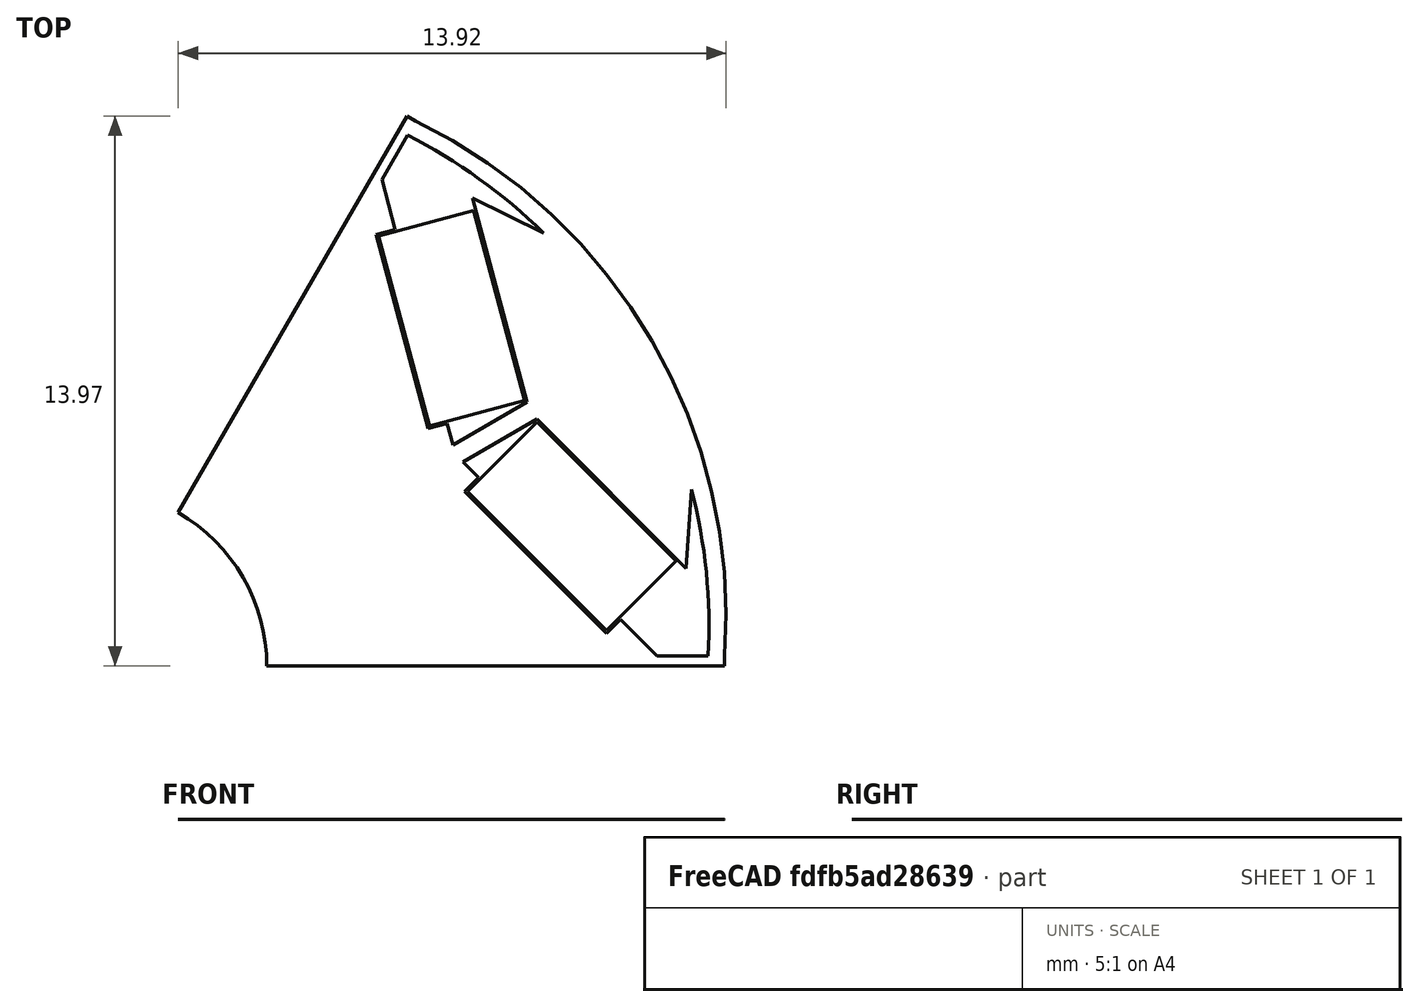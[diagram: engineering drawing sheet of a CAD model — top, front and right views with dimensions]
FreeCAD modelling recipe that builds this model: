
FCSTD DOCUMENT  (FreeCAD 0.18R4 (GitTag))
Label: vrotor
License: All rights reserved
LicenseURL: http://en.wikipedia.org/wiki/All_rights_reserved
objects: Sketcher::SketchObject×7, Surface::Filling×7, PartDesign::Body×2, Part::Cut×2, Spreadsheet::Sheet×1, Part::MultiFuse×1
note: 19 computed .brp shape members not serialized (recipe doc carries the construction recipe); baked Part::Feature solids carry a one-line shape summary decoded from their .brp

FEATURE [Spreadsheet::Sheet] Spreadsheet  label="Variables"
  cells = A2=poleNumber; B2(poleNumber)=6; A3=outerDiameter; B3(outerDiameter)=33; D3=Calc Value; A4=innerDiameter; B4(innerDiameter)=9; D4=Input Value; A5=stackLength; B5(stackLength)=20; D5=Used; A6=stackingFactor; B6(stackingFactor)=0.95; A7=embrace; B7(embrace)=70; A8=contourRatio; B8(contourRatio)=85; A9=magnetAirgap; B9(magnetAirgap)=0.05; A10=poleSeparation; B10(poleSeparation)=0.5; A11=magnetWidth; B11(magnetWidth)=5; A12=magnetHeight; B12(magnetHeight)=2.5; A13=rib; B13(rib)=0.5; A14=bridgeCurved; B14(bridgeCurved)=0.5; A15=cutTop; B15(cutTop)=0.01; A16=cutBottom; B16(cutBottom)=0.5; A17=segmentAngle; B17(segmentAngle)==360 / poleNumber; A18=movePocketInwards; B18(movePocketInwards)=0.5; A19=cuttingThickness; B19(cuttingThickness)=0.1; A20=magnetLength; B20(magnetLength)==stackLength; A21=cut; B21(cut)=0.2; A22=ribShaft; B22(ribShaft)=0.5; A23=magnetEmbrace; B23(magnetEmbrace)=75; A24=magnetContourRatio; B24(magnetContourRatio)=95; A25=axialMisalignment; B25(axialMisalignment)=0.5; A26=magnetAngle; B26(magnetAngle)=150; A27=magnetContactRatio; B27(magnetContactRatio)=65
FEATURE [Sketcher::SketchObject] Sketch003  label="RotorPoleSketch"
  MapMode = 5
  Support = -> [XY_Plane]
  expr: Constraints[14] = Variables.innerDiameter / 2
  expr: Constraints[55] = Variables.outerDiameter / 2 * Variables.contourRatio / 100
  expr: Constraints[73] = Variables.movePocketInwards
  expr: Constraints[59] = Variables.poleSeparation / 2
  expr: Constraints[106] = Variables.magnetHeight + 2 * Variables.magnetAirgap
  expr: Constraints[23] = Variables.outerDiameter / 2 * Variables.contourRatio / 100
  expr: Constraints[90] = Variables.cutTop
  expr: Constraints[71] = Variables.segmentAngle * Variables.embrace / 100
  expr: Constraints[15] = Variables.outerDiameter / 2
  expr: Constraints[103] = Variables.cutBottom
  expr: Constraints[58] = Variables.bridgeCurved
  expr: Constraints[114] = Variables.outerDiameter / 2 * Variables.contourRatio / 100 - Variables.bridgeCurved
  expr: Constraints[51] = Variables.rib / 2
  expr: Constraints[43] = Variables.rib / 2
  expr: Constraints[0] = Variables.segmentAngle
  expr: Constraints[18] = Variables.segmentAngle / 2
  expr: Constraints[91] = Variables.magnetWidth + Variables.magnetAirgap * 2
  expr: Constraints[116] = Variables.outerDiameter / 2 * Variables.contourRatio / 100 - Variables.bridgeCurved
  expr: Constraints[27] = Variables.poleSeparation / 2
  sketch-geometry (40):
    g0: LineSegment [constr] StartX=4.5 StartY=0 StartZ=0 EndX=16.5 EndY=0 EndZ=0
    g1: LineSegment [constr] StartX=2.25 StartY=3.89711 StartZ=0 EndX=8.25 EndY=14.2894 EndZ=0
    g2: LineSegment [constr] StartX=0 StartY=0 StartZ=0 EndX=4.5 EndY=0 EndZ=0
    g3: LineSegment [constr] StartX=0 StartY=0 StartZ=0 EndX=2.25 EndY=3.89711 EndZ=0
    g4: ArcOfCircle [constr] CenterX=0 CenterY=0 CenterZ=0 NormalX=0 NormalY=0 NormalZ=1 AngleXU=0 Radius=16.5 StartAngle=0 EndAngle=1.0472
    g5: ArcOfCircle CenterX=0 CenterY=0 CenterZ=0 NormalX=0 NormalY=0 NormalZ=1 AngleXU=0 Radius=4.5 StartAngle=0 EndAngle=1.0472
    g6: LineSegment [constr] StartX=0 StartY=0 StartZ=0 EndX=14.2894 EndY=8.25 EndZ=0
    g7: ArcOfCircle [constr] CenterX=2.14341 CenterY=1.2375 CenterZ=0 NormalX=0 NormalY=0 NormalZ=1 AngleXU=0 Radius=14.025 StartAngle=6.19484 EndAngle=7.41873
    g8: LineSegment StartX=8.0668 StartY=13.9721 StartZ=0 EndX=8.28331 EndY=13.8471 EndZ=0
    g9: LineSegment StartX=16.1336 StartY=0 StartZ=0 EndX=16.1336 EndY=0.25 EndZ=0
    g10: ArcOfCircle CenterX=2.14341 CenterY=1.2375 CenterZ=0 NormalX=0 NormalY=0 NormalZ=1 AngleXU=0 Radius=14.025 StartAngle=6.21272 EndAngle=7.40085
    g11: LineSegment StartX=2.25 StartY=3.89711 StartZ=0 EndX=8.0668 EndY=13.9721 EndZ=0
    g12: LineSegment StartX=4.5 StartY=0 StartZ=0 EndX=16.1336 EndY=0 EndZ=0
    g13: LineSegment [constr] StartX=8.46556 StartY=14.1628 StartZ=0 EndX=2.46303 EndY=3.7661 EndZ=0
    g14: LineSegment [constr] StartX=2.46303 StartY=3.7661 StartZ=0 EndX=2.24653 EndY=3.8911 EndZ=0
    g15: LineSegment [constr] StartX=4.49305 StartY=0.25 StartZ=0 EndX=16.4981 EndY=0.25 EndZ=0
    g16: LineSegment [constr] StartX=4.49305 StartY=0.25 StartZ=0 EndX=4.49305 EndY=0 EndZ=0
    g17: ArcOfCircle [constr] CenterX=1.7104 CenterY=0.9875 CenterZ=0 NormalX=0 NormalY=0 NormalZ=1 AngleXU=0 Radius=14.025 StartAngle=6.21272 EndAngle=7.40085
    g18: LineSegment [constr] StartX=2.14341 StartY=1.2375 StartZ=0 EndX=1.7104 EndY=0.9875 EndZ=0
    g19: LineSegment [constr] StartX=15.6558 StartY=2.47964 StartZ=0 EndX=15.1558 EndY=2.47964 EndZ=0
    g20: LineSegment [constr] StartX=15.1558 StartY=2.47964 StartZ=0 EndX=9.72533 EndY=11.8855 EndZ=0
    g21: LineSegment [constr] StartX=9.72533 StartY=11.8855 StartZ=0 EndX=9.97533 EndY=12.3185 EndZ=0
    g22: LineSegment [constr] StartX=0 StartY=0 StartZ=0 EndX=15.6558 EndY=2.47964 EndZ=0
    g23: LineSegment [constr] StartX=0 StartY=0 StartZ=0 EndX=9.97533 EndY=12.3185 EndZ=0
    g24: ArcOfCircle [constr] CenterX=2.00505 CenterY=1.39146 CenterZ=0 NormalX=0 NormalY=0 NormalZ=1 AngleXU=0 Radius=13.525 StartAngle=0.940605 EndAngle=1.10569
    g25: ArcOfCircle [constr] CenterX=2.20756 CenterY=1.0407 CenterZ=0 NormalX=0 NormalY=0 NormalZ=1 AngleXU=0 Radius=13.525 StartAngle=6.22469 EndAngle=6.38978
    g26: LineSegment [constr] StartX=9.72533 StartY=11.8855 StartZ=0 EndX=11.1656 EndY=9.39093 EndZ=0
    g27: LineSegment [constr] StartX=11.1656 StartY=9.39093 StartZ=0 EndX=11.1742 EndY=9.39593 EndZ=0
    g28: LineSegment [constr] StartX=11.1742 StartY=9.39593 StartZ=0 EndX=13.7242 EndY=4.9792 EndZ=0
    g29: LineSegment [constr] StartX=13.7242 StartY=4.9792 StartZ=0 EndX=13.7156 EndY=4.9742 EndZ=0
    g30: LineSegment [constr] StartX=13.7156 StartY=4.9742 StartZ=0 EndX=15.1558 EndY=2.47964 EndZ=0
    g31: LineSegment [constr] StartX=7.23138 StartY=12.0251 StartZ=0 EndX=14.0298 EndY=0.25 EndZ=0
    g32: LineSegment [constr] StartX=9.35557 StartY=8.34593 StartZ=0 EndX=8.92256 EndY=8.09593 EndZ=0
    g33: LineSegment [constr] StartX=8.92256 StartY=8.09593 StartZ=0 EndX=11.4726 EndY=3.6792 EndZ=0
    g34: LineSegment [constr] StartX=11.4726 StartY=3.6792 StartZ=0 EndX=11.9056 EndY=3.9292 EndZ=0
    g35: LineSegment [constr] StartX=11.4726 StartY=3.6792 StartZ=0 EndX=13.7242 EndY=4.9792 EndZ=0
    g36: LineSegment [constr] StartX=9.35557 StartY=8.34593 StartZ=0 EndX=7.23138 EndY=12.0251 EndZ=0
    g37: LineSegment [constr] StartX=11.9056 StartY=3.9292 StartZ=0 EndX=14.0298 EndY=0.25 EndZ=0
    g38: LineSegment [constr] StartX=7.23138 StartY=12.0251 StartZ=0 EndX=8.07122 EndY=13.4798 EndZ=0
    g39: LineSegment [constr] StartX=14.0298 StartY=0.25 StartZ=0 EndX=15.7094 EndY=0.25 EndZ=0
  constraints (117):
    c: Angle(g0,g1) = 1.0472
    c: Coincident(g2,g-1)
    c: Coincident(g2,g0)
    c: Coincident(g3,g2)
    c: Coincident(g3,g1)
    c: Parallel(g2,g0)
    c: Parallel(g3,g1)
    c: Coincident(g4,g-1)
    c: Coincident(g4,g0)
    c: Coincident(g4,g1)
    c: Coincident(g5,g4)
    c: Coincident(g5,g1)
    c: Coincident(g5,g0)
    c: Angle(g-1,g2) = 0
    c: Radius(g5) = 4.5
    c: Radius(g4) = 16.5
    c: Coincident(g6,g5)
    c: PointOnObject(g6,g4)
    c: Angle(g-1,g6) = 0.523599
    c: PointOnObject(g7,g1)
    c: PointOnObject(g7,g0)
    c: PointOnObject(g6,g7)
    c: PointOnObject(g7,g6)
    c: Radius(g7) = 14.025
    c: PointOnObject(g8,g1)
    c: PointOnObject(g8,g7)
    c: Angle(g1,g8) = 1.5708
    c: Distance(g8) = 0.25
    c: PointOnObject(g9,g0)
    c: PointOnObject(g9,g7)
    c: Angle(g9,g0) = 1.5708
    c: Coincident(g10,g8)
    c: Coincident(g10,g9)
    c: PointOnObject(g6,g10)
    c: Coincident(g11,g5)
    c: Coincident(g11,g8)
    c: Coincident(g12,g5)
    c: Coincident(g12,g9)
    c: PointOnObject(g13,g4)
    c: PointOnObject(g13,g5)
    c: Coincident(g14,g13)
    c: PointOnObject(g14,g11)
    c: Angle(g13,g14) = 1.5708
    c: Distance(g14) = 0.25
    c: Parallel(g11,g13)
    c: PointOnObject(g15,g5)
    c: PointOnObject(g15,g4)
    c: Parallel(g15,g2)
    c: Coincident(g16,g15)
    c: PointOnObject(g16,g2)
    c: Angle(g16,g15) = 1.5708
    c: Distance(g16) = 0.25
    c: PointOnObject(g17,g6)
    c: PointOnObject(g17,g11)
    c: PointOnObject(g17,g12)
    c: Radius(g17) = 14.025
    c: Coincident(g18,g10)
    c: Coincident(g18,g17)
    c: Distance(g17,g10) = 0.5
    c: DistanceY(g9,g9) = 0.25
    c: PointOnObject(g38,g13)
    c: PointOnObject(g39,g15)
    c: PointOnObject(g19,g17)
    c: Horizontal(g19)
    c: Coincident(g20,g19)
    c: Coincident(g21,g20)
    c: Coincident(g22,g5)
    c: Coincident(g22,g19)
    c: Coincident(g23,g5)
    c: Coincident(g23,g21)
    c: Symmetric(g21,g19,g6)
    c: Angle(g22,g23) = 0.733038
    c: Parallel(g21,g11)
    c: DistanceX(g19,g19) = 0.5
    c: Equal(g19,g21)
    c: Coincident(g24,g21)
    c: Tangent(g24,g17)
    c: Coincident(g25,g19)
    c: Tangent(g25,g17)
    c: Coincident(g26,g21)
    c: PointOnObject(g26,g20)
    c: Coincident(g27,g26)
    c: Coincident(g28,g27)
    c: Coincident(g29,g28)
    c: Coincident(g30,g29)
    c: Coincident(g30,g19)
    c: Angle(g29,g20) = 1.5708
    c: Perpendicular(g29,g28)
    c: Angle(g27,g28) = 1.5708
    c: Symmetric(g29,g26,g6)
    c: Distance(g27) = 0.01
    c: Distance(g28) = 5.1
    c: PointOnObject(g31,g13)
    c: PointOnObject(g31,g15)
    c: Parallel(g31,g20)
    c: PointOnObject(g32,g31)
    c: Coincident(g33,g32)
    c: Coincident(g34,g33)
    c: PointOnObject(g34,g31)
    c: Angle(g33,g32) = 1.5708
    c: Angle(g34,g33) = 1.5708
    c: Symmetric(g32,g33,g6)
    c: Equal(g33,g28)
    c: Distance(g34) = 0.5
    c: Coincident(g35,g33)
    c: Coincident(g35,g28)
    c: Distance(g35) = 2.6
    c: Coincident(g36,g32)
    c: Coincident(g36,g31)
    c: Coincident(g37,g34)
    c: Coincident(g37,g31)
    c: Coincident(g38,g36)
    c: Coincident(g39,g37)
    c: Coincident(g24,g38)
    c: Radius(g24) = 13.525
    c: Coincident(g25,g39)
    c: Radius(g25) = 13.525
FEATURE [Sketcher::SketchObject] Sketch004  label="BoundingBox"
  MapMode = 5
  Support = -> [XY_Plane]
  expr: Constraints[8] = Variables.outerDiameter
  sketch-geometry (6):
    g0: LineSegment StartX=-16.5 StartY=-16.5 StartZ=0 EndX=16.5 EndY=-16.5 EndZ=0
    g1: LineSegment StartX=16.5 StartY=-16.5 StartZ=0 EndX=16.5 EndY=16.5 EndZ=0
    g2: LineSegment StartX=16.5 StartY=16.5 StartZ=0 EndX=-16.5 EndY=16.5 EndZ=0
    g3: LineSegment StartX=-16.5 StartY=16.5 StartZ=0 EndX=-16.5 EndY=-16.5 EndZ=0
    g4: LineSegment [constr] StartX=-16.5 StartY=-16.5 StartZ=0 EndX=16.5 EndY=16.5 EndZ=0
    g5: GeomPoint X=0 Y=0 Z=0
  constraints (14):
    c: Coincident(g0,g1)
    c: Coincident(g1,g2)
    c: Coincident(g2,g3)
    c: Coincident(g3,g0)
    c: Horizontal(g0)
    c: Horizontal(g2)
    c: Vertical(g1)
    c: Vertical(g3)
    c: DistanceY(g1,g1) = 33
    c: Equal(g2,g1)
    c: Coincident(g4,g0)
    c: Coincident(g4,g1)
    c: Symmetric(g0,g1,g5)
    c: Coincident(g-1,g5)
FEATURE [Sketcher::SketchObject] Sketch005  label="RotorSideSketch"
  MapMode = 5
  Support = -> [XY_Plane001]
  expr: Constraints[23] = Variables.stackLength / 2 - Variables.axialMisalignment
  expr: Constraints[19] = Variables.innerDiameter / 2
  expr: Constraints[22] = Variables.stackLength / 2 - Variables.axialMisalignment
  expr: Constraints[9] = Variables.outerDiameter / 2
  expr: Constraints[8] = Variables.innerDiameter / 2
  expr: Constraints[7] = Variables.stackLength
  sketch-geometry (8):
    g0: LineSegment StartX=-9.5 StartY=4.5 StartZ=0 EndX=10.5 EndY=4.5 EndZ=0
    g1: LineSegment StartX=10.5 StartY=4.5 StartZ=0 EndX=10.5 EndY=16.5 EndZ=0
    g2: LineSegment StartX=10.5 StartY=16.5 StartZ=0 EndX=-9.5 EndY=16.5 EndZ=0
    g3: LineSegment StartX=-9.5 StartY=16.5 StartZ=0 EndX=-9.5 EndY=4.5 EndZ=0
    g4: LineSegment StartX=-9.5 StartY=-4.5 StartZ=0 EndX=10.5 EndY=-4.5 EndZ=0
    g5: LineSegment StartX=10.5 StartY=-4.5 StartZ=0 EndX=10.5 EndY=-16.5 EndZ=0
    g6: LineSegment StartX=10.5 StartY=-16.5 StartZ=0 EndX=-9.5 EndY=-16.5 EndZ=0
    g7: LineSegment StartX=-9.5 StartY=-16.5 StartZ=0 EndX=-9.5 EndY=-4.5 EndZ=0
  constraints (24):
    c: Coincident(g0,g1)
    c: Coincident(g1,g2)
    c: Coincident(g2,g3)
    c: Coincident(g3,g0)
    c: Horizontal(g0)
    c: Vertical(g1)
    c: Vertical(g3)
    c: DistanceX(g2,g2) = 20
    c: DistanceY(g-1,g0) = 4.5
    c: DistanceY(g-1,g1) = 16.5
    c: Coincident(g4,g5)
    c: Coincident(g5,g6)
    c: Coincident(g6,g7)
    c: Coincident(g7,g4)
    c: Horizontal(g4)
    c: Vertical(g5)
    c: Vertical(g7)
    c: Equal(g4,g0)
    c: Equal(g7,g3)
    c: DistanceY(g4,g-1) = 4.5
    c: Horizontal(g2)
    c: Horizontal(g6)
    c: DistanceX(g0,g-1) = 9.5
    c: DistanceX(g4,g-1) = 9.5
FEATURE [Sketcher::SketchObject] Sketch006  label="MagnetSideSketch"
  ExternalGeometry = -> [Sketch005]
  MapMode = 5
  Support = -> [XY_Plane001]
  expr: Constraints[23] = Variables.stackLength / 2 - Variables.axialMisalignment
  expr: Constraints[12] = Variables.magnetHeight / 2
  expr: Constraints[8] = Variables.magnetHeight
  expr: Constraints[7] = Variables.magnetLength
  sketch-geometry (9):
    g0: LineSegment StartX=-9.5 StartY=12.75 StartZ=0 EndX=10.5 EndY=12.75 EndZ=0
    g1: LineSegment StartX=10.5 StartY=12.75 StartZ=0 EndX=10.5 EndY=15.25 EndZ=0
    g2: LineSegment StartX=10.5 StartY=15.25 StartZ=0 EndX=-9.5 EndY=15.25 EndZ=0
    g3: LineSegment StartX=-9.5 StartY=15.25 StartZ=0 EndX=-9.5 EndY=12.75 EndZ=0
    g4: LineSegment [constr] StartX=10.5 StartY=15.25 StartZ=0 EndX=10.5 EndY=16.5 EndZ=0
    g5: LineSegment StartX=-9.5 StartY=-15.25 StartZ=0 EndX=10.5 EndY=-15.25 EndZ=0
    g6: LineSegment StartX=10.5 StartY=-15.25 StartZ=0 EndX=10.5 EndY=-12.75 EndZ=0
    g7: LineSegment StartX=10.5 StartY=-12.75 StartZ=0 EndX=-9.5 EndY=-12.75 EndZ=0
    g8: LineSegment StartX=-9.5 StartY=-12.75 StartZ=0 EndX=-9.5 EndY=-15.25 EndZ=0
  constraints (25):
    c: Coincident(g0,g1)
    c: Coincident(g1,g2)
    c: Coincident(g2,g3)
    c: Coincident(g3,g0)
    c: Horizontal(g0)
    c: Vertical(g1)
    c: Vertical(g3)
    c: DistanceX(g2,g2) = 20
    c: DistanceY(g1,g1) = 2.5
    c: Coincident(g4,g1)
    c: PointOnObject(g4,g-3)
    c: Angle(g4,g2) = 1.5708
    c: DistanceY(g4,g4) = 1.25
    c: Coincident(g5,g6)
    c: Coincident(g6,g7)
    c: Coincident(g7,g8)
    c: Coincident(g8,g5)
    c: Horizontal(g5)
    c: Vertical(g6)
    c: Vertical(g8)
    c: Symmetric(g7,g0,g-1)
    c: Symmetric(g6,g0,g-1)
    c: Equal(g8,g3)
    c: DistanceX(g0,g-1) = 9.5
    c: Horizontal(g2)
FEATURE [PartDesign::Body] Body001  label="SideView"
  Group = -> [Sketch005,Sketch006]
  Origin = -> Origin001
FEATURE [Surface::Filling] Surface  label="RotorPoleSketch_Surface"
  Anisotropy = false
  BoundaryEdges = -> [Sketch003]
  BoundaryOrder = [0,0,0,0,0,0]
  Degree = 3
  Iterations = 2
  MaximumDegree = 8
  MaximumSegments = 9
  PointsOnCurve = 15
  TolAngular = 0.01
  TolCurvature = 0.1
  Tolerance2d = 1e-05
  Tolerance3d = 0.0001
FEATURE [Sketcher::SketchObject] Sketch007  label="PocketSketch"
  MapMode = 5
  Support = -> [XY_Plane]
  expr: Constraints[123] = Variables.rib / 2
  expr: Constraints[93] = Variables.magnetAngle
  expr: Constraints[78] = 0.5 * Variables.segmentAngle * Variables.embrace / 100 * Variables.magnetContactRatio / 100
  expr: Constraints[51] = Variables.rib / 2
  expr: Constraints[27] = Variables.poleSeparation / 2
  expr: Constraints[14] = Variables.innerDiameter / 2
  expr: Constraints[55] = Variables.outerDiameter / 2 * Variables.contourRatio / 100
  expr: Constraints[115] = Variables.cutBottom
  expr: Constraints[103] = Variables.magnetHeight + Variables.magnetAirgap * 2 - Variables.cutBottom
  expr: Constraints[58] = Variables.bridgeCurved
  expr: Constraints[69] = Variables.segmentAngle * Variables.embrace / 100
  expr: Constraints[71] = Variables.movePocketInwards
  expr: Constraints[15] = Variables.outerDiameter / 2
  expr: Constraints[59] = Variables.poleSeparation / 2
  expr: Constraints[116] = Variables.magnetWidth + Variables.magnetAirgap * 2
  expr: Constraints[23] = Variables.outerDiameter / 2 * Variables.contourRatio / 100
  expr: Constraints[43] = Variables.rib / 2
  expr: Constraints[18] = Variables.segmentAngle / 2
  expr: Constraints[0] = Variables.segmentAngle
  sketch-geometry (54):
    g0: LineSegment [constr] StartX=4.5 StartY=0 StartZ=0 EndX=16.5 EndY=0 EndZ=0
    g1: LineSegment [constr] StartX=2.25 StartY=3.89711 StartZ=0 EndX=8.25 EndY=14.2894 EndZ=0
    g2: LineSegment [constr] StartX=0 StartY=0 StartZ=0 EndX=4.5 EndY=0 EndZ=0
    g3: LineSegment [constr] StartX=0 StartY=0 StartZ=0 EndX=2.25 EndY=3.89711 EndZ=0
    g4: ArcOfCircle [constr] CenterX=0 CenterY=0 CenterZ=0 NormalX=0 NormalY=0 NormalZ=1 AngleXU=0 Radius=16.5 StartAngle=0 EndAngle=1.0472
    g5: ArcOfCircle [constr] CenterX=0 CenterY=0 CenterZ=0 NormalX=0 NormalY=0 NormalZ=1 AngleXU=0 Radius=4.5 StartAngle=0 EndAngle=1.0472
    g6: LineSegment [constr] StartX=0 StartY=0 StartZ=0 EndX=14.2894 EndY=8.25 EndZ=0
    g7: ArcOfCircle [constr] CenterX=2.14341 CenterY=1.2375 CenterZ=0 NormalX=0 NormalY=0 NormalZ=1 AngleXU=0 Radius=14.025 StartAngle=6.19484 EndAngle=7.41873
    g8: LineSegment [constr] StartX=8.0668 StartY=13.9721 StartZ=0 EndX=8.28331 EndY=13.8471 EndZ=0
    g9: LineSegment [constr] StartX=16.1336 StartY=0 StartZ=0 EndX=16.1336 EndY=0.25 EndZ=0
    g10: ArcOfCircle [constr] CenterX=2.14341 CenterY=1.2375 CenterZ=0 NormalX=0 NormalY=0 NormalZ=1 AngleXU=0 Radius=14.025 StartAngle=6.21272 EndAngle=7.40085
    g11: LineSegment [constr] StartX=2.25 StartY=3.89711 StartZ=0 EndX=8.0668 EndY=13.9721 EndZ=0
    g12: LineSegment [constr] StartX=4.5 StartY=0 StartZ=0 EndX=16.1336 EndY=0 EndZ=0
    g13: LineSegment [constr] StartX=8.46556 StartY=14.1628 StartZ=0 EndX=2.46303 EndY=3.7661 EndZ=0
    g14: LineSegment [constr] StartX=2.46303 StartY=3.7661 StartZ=0 EndX=2.24653 EndY=3.8911 EndZ=0
    g15: LineSegment [constr] StartX=4.49305 StartY=0.25 StartZ=0 EndX=16.4981 EndY=0.25 EndZ=0
    g16: LineSegment [constr] StartX=4.49305 StartY=0.25 StartZ=0 EndX=4.49305 EndY=0 EndZ=0
    g17: ArcOfCircle [constr] CenterX=1.7104 CenterY=0.9875 CenterZ=0 NormalX=0 NormalY=0 NormalZ=1 AngleXU=0 Radius=14.025 StartAngle=6.21272 EndAngle=7.40085
    g18: LineSegment [constr] StartX=2.14341 StartY=1.2375 StartZ=0 EndX=1.7104 EndY=0.9875 EndZ=0
    g19: LineSegment [constr] StartX=15.6558 StartY=2.47964 StartZ=0 EndX=15.1558 EndY=2.47964 EndZ=0
    g20: LineSegment [constr] StartX=15.1558 StartY=2.47964 StartZ=0 EndX=9.72533 EndY=11.8855 EndZ=0
    g21: LineSegment [constr] StartX=9.72533 StartY=11.8855 StartZ=0 EndX=9.97533 EndY=12.3185 EndZ=0
    g22: LineSegment [constr] StartX=0 StartY=0 StartZ=0 EndX=15.6558 EndY=2.47964 EndZ=0
    g23: LineSegment [constr] StartX=0 StartY=0 StartZ=0 EndX=9.97533 EndY=12.3185 EndZ=0
    g24: ArcOfCircle [constr] CenterX=1.7104 CenterY=0.9875 CenterZ=0 NormalX=0 NormalY=0 NormalZ=1 AngleXU=0 Radius=14.025 StartAngle=0.252123 EndAngle=0.795074
    g25: LineSegment [constr] StartX=0 StartY=0 StartZ=0 EndX=15.292 EndY=4.48618 EndZ=0
    g26: LineSegment StartX=11.5311 StartY=11.0002 StartZ=0 EndX=9.72533 EndY=11.8855 EndZ=0
    g27: LineSegment StartX=15.292 StartY=4.48618 StartZ=0 EndX=15.1558 EndY=2.47964 EndZ=0
    g28: ArcOfCircle CenterX=1.7104 CenterY=0.9875 CenterZ=0 NormalX=0 NormalY=0 NormalZ=1 AngleXU=0 Radius=14.025 StartAngle=0.795074 EndAngle=1.09981
    g29: ArcOfCircle CenterX=1.7104 CenterY=0.9875 CenterZ=0 NormalX=0 NormalY=0 NormalZ=1 AngleXU=0 Radius=14.025 StartAngle=6.23058 EndAngle=6.53531
    g30: LineSegment [constr] StartX=9.72533 StartY=11.8855 StartZ=0 EndX=11.1804 EndY=6.45502 EndZ=0
    g31: LineSegment [constr] StartX=11.1804 StartY=6.45502 StartZ=0 EndX=15.1558 EndY=2.47964 EndZ=0
    g32: LineSegment [constr] StartX=7.4243 StartY=12.3593 StartZ=0 EndX=9.29761 EndY=5.36798 EndZ=0
    g33: LineSegment [constr] StartX=9.29761 StartY=5.36798 StartZ=0 EndX=14.4156 EndY=0.25 EndZ=0
    g34: LineSegment [constr] StartX=7.4243 StartY=12.3593 StartZ=0 EndX=9.45274 EndY=12.9028 EndZ=0
    g35: LineSegment StartX=8.0745 StartY=13.4855 StartZ=0 EndX=7.4243 EndY=12.3593 EndZ=0
    g36: LineSegment StartX=7.4243 StartY=12.3593 StartZ=0 EndX=7.76501 EndY=11.0877 EndZ=0
    g37: LineSegment StartX=7.76501 StartY=11.0877 StartZ=0 EndX=7.28205 EndY=10.9583 EndZ=0
    g38: LineSegment StartX=7.28205 StartY=10.9583 StartZ=0 EndX=8.60202 EndY=6.03209 EndZ=0
    g39: LineSegment StartX=8.60202 StartY=6.03209 StartZ=0 EndX=9.08499 EndY=6.1615 EndZ=0
    g40: LineSegment StartX=9.23062 StartY=5.61798 StartZ=0 EndX=11.1134 EndY=6.70502 EndZ=0
    g41: LineSegment [constr] StartX=9.23062 StartY=5.61798 StartZ=0 EndX=9.35562 EndY=5.40147 EndZ=0
    g42: LineSegment [constr] StartX=9.08499 StartY=6.1615 StartZ=0 EndX=11.1134 EndY=6.70502 EndZ=0
    g43: LineSegment StartX=9.08499 StartY=6.1615 StartZ=0 EndX=9.23062 EndY=5.61798 EndZ=0
    g44: LineSegment StartX=9.72533 StartY=11.8855 StartZ=0 EndX=11.1134 EndY=6.70502 EndZ=0
    g45: LineSegment StartX=9.48062 StartY=5.18496 StartZ=0 EndX=9.87851 EndY=4.78708 EndZ=0
    g46: LineSegment StartX=9.87851 StartY=4.78708 StartZ=0 EndX=9.52495 EndY=4.43353 EndZ=0
    g47: LineSegment StartX=9.52495 StartY=4.43353 StartZ=0 EndX=13.1312 EndY=0.827282 EndZ=0
    g48: LineSegment StartX=14.4156 StartY=0.25 StartZ=0 EndX=14.4156 EndY=0.25 EndZ=0
    g49: LineSegment StartX=13.1312 StartY=0.827282 StartZ=0 EndX=13.4848 EndY=1.18084 EndZ=0
    g50: LineSegment StartX=13.4848 StartY=1.18084 StartZ=0 EndX=14.4156 EndY=0.25 EndZ=0
    g51: LineSegment StartX=14.4156 StartY=0.25 StartZ=0 EndX=15.716 EndY=0.25 EndZ=0
    g52: LineSegment StartX=15.1558 StartY=2.47964 StartZ=0 EndX=11.3634 EndY=6.272 EndZ=0
    g53: LineSegment StartX=11.3634 StartY=6.272 StartZ=0 EndX=9.48062 EndY=5.18496 EndZ=0
  constraints (149):
    c: Angle(g0,g1) = 1.0472
    c: Coincident(g2,g-1)
    c: Coincident(g2,g0)
    c: Coincident(g3,g2)
    c: Coincident(g3,g1)
    c: Parallel(g2,g0)
    c: Parallel(g3,g1)
    c: Coincident(g4,g-1)
    c: Coincident(g4,g0)
    c: Coincident(g4,g1)
    c: Coincident(g5,g4)
    c: Coincident(g5,g1)
    c: Coincident(g5,g0)
    c: Angle(g-1,g2) = 0
    c: Radius(g5) = 4.5
    c: Radius(g4) = 16.5
    c: Coincident(g6,g5)
    c: PointOnObject(g6,g4)
    c: Angle(g-1,g6) = 0.523599
    c: PointOnObject(g7,g1)
    c: PointOnObject(g7,g0)
    c: PointOnObject(g6,g7)
    c: PointOnObject(g7,g6)
    c: Radius(g7) = 14.025
    c: PointOnObject(g8,g1)
    c: PointOnObject(g8,g7)
    c: Angle(g1,g8) = 1.5708
    c: Distance(g8) = 0.25
    c: PointOnObject(g9,g0)
    c: PointOnObject(g9,g7)
    c: Angle(g9,g0) = 1.5708
    c: Coincident(g10,g8)
    c: Coincident(g10,g9)
    c: PointOnObject(g6,g10)
    c: Coincident(g11,g5)
    c: Coincident(g11,g8)
    c: Coincident(g12,g5)
    c: Coincident(g12,g9)
    c: PointOnObject(g13,g4)
    c: PointOnObject(g13,g5)
    c: Coincident(g14,g13)
    c: PointOnObject(g14,g11)
    c: Angle(g13,g14) = 1.5708
    c: Distance(g14) = 0.25
    c: Parallel(g11,g13)
    c: PointOnObject(g15,g5)
    c: PointOnObject(g15,g4)
    c: Parallel(g15,g2)
    c: Coincident(g16,g15)
    c: PointOnObject(g16,g2)
    c: Angle(g16,g15) = 1.5708
    c: Distance(g16) = 0.25
    c: PointOnObject(g17,g6)
    c: PointOnObject(g17,g11)
    c: PointOnObject(g17,g12)
    c: Radius(g17) = 14.025
    c: Coincident(g18,g10)
    c: Coincident(g18,g17)
    c: Distance(g17,g10) = 0.5
    c: DistanceY(g9,g9) = 0.25
    c: PointOnObject(g19,g17)
    c: Horizontal(g19)
    c: Coincident(g20,g19)
    c: Coincident(g21,g20)
    c: Coincident(g22,g5)
    c: Coincident(g22,g19)
    c: Coincident(g23,g5)
    c: Coincident(g23,g21)
    c: Symmetric(g21,g19,g6)
    c: Angle(g22,g23) = 0.733038
    c: Parallel(g21,g11)
    c: DistanceX(g19,g19) = 0.5
    c: Equal(g19,g21)
    c: PointOnObject(g24,g17)
    c: Tangent(g24,g17)
    c: Symmetric(g24,g24,g6)
    c: Coincident(g25,g-1)
    c: Coincident(g25,g24)
    c: Angle(g25,g6) = 0.238237
    c: Coincident(g26,g24)
    c: Coincident(g26,g20)
    c: Coincident(g27,g24)
    c: Coincident(g27,g19)
    c: Coincident(g28,g24)
    c: PointOnObject(g28,g13)
    c: Coincident(g28,g24)
    c: Coincident(g29,g24)
    c: PointOnObject(g29,g15)
    c: Coincident(g29,g24)
    c: Coincident(g30,g26)
    c: PointOnObject(g30,g6)
    c: Coincident(g31,g30)
    c: Coincident(g31,g27)
    c: Angle(g31,g30) = 2.61799
    c: PointOnObject(g32,g13)
    c: PointOnObject(g32,g6)
    c: Coincident(g33,g32)
    c: PointOnObject(g33,g15)
    c: Parallel(g32,g30)
    c: Equal(g33,g32)
    c: Coincident(g34,g32)
    c: PointOnObject(g34,g30)
    c: Angle(g32,g34) = 1.5708
    c: Distance(g34) = 2.1
    c: Coincident(g35,g28)
    c: Coincident(g35,g32)
    c: Coincident(g36,g35)
    c: PointOnObject(g36,g32)
    c: Coincident(g37,g36)
    c: Coincident(g38,g37)
    c: Coincident(g39,g38)
    c: PointOnObject(g39,g32)
    c: Angle(g36,g37) = 1.5708
    c: Angle(g39,g38) = 1.5708
    c: Parallel(g38,g32)
    c: Distance(g37) = 0.5
    c: Distance(g38) = 5.1
    c: PointOnObject(g40,g32)
    c: PointOnObject(g40,g30)
    c: Parallel(g40,g6)
    c: Coincident(g41,g40)
    c: PointOnObject(g41,g6)
    c: Angle(g6,g41) = 1.5708
    c: Distance(g41) = 0.25
    c: Coincident(g42,g39)
    c: Coincident(g42,g40)
    c: Angle(g42,g32) = 1.5708
    c: Coincident(g43,g39)
    c: Coincident(g43,g40)
    c: Coincident(g44,g26)
    c: Coincident(g44,g40)
    c: Coincident(g46,g45)
    c: Coincident(g47,g46)
    c: Coincident(g48,g33)
    c: Symmetric(g45,g40,g6)
    c: Symmetric(g45,g39,g6)
    c: Symmetric(g46,g38,g6)
    c: Symmetric(g47,g37,g6)
    c: Symmetric(g48,g35,g6)
    c: Coincident(g49,g47)
    c: Coincident(g50,g49)
    c: Coincident(g50,g48)
    c: Symmetric(g49,g36,g6)
    c: Coincident(g51,g48)
    c: Coincident(g51,g29)
    c: Coincident(g52,g27)
    c: Symmetric(g52,g40,g6)
    c: Coincident(g53,g52)
    c: Coincident(g53,g45)
FEATURE [Surface::Filling] Surface001  label="Pocket_Surface1"
  Anisotropy = false
  BoundaryEdges = -> [Sketch007]
  BoundaryOrder = [0,0,0,0,0,0,0,0,0,0]
  Degree = 3
  Iterations = 2
  MaximumDegree = 8
  MaximumSegments = 9
  PointsOnCurve = 15
  TolAngular = 0.01
  TolCurvature = 0.1
  Tolerance2d = 1e-05
  Tolerance3d = 0.0001
FEATURE [Surface::Filling] Surface002  label="Pocket_Surface2"
  Anisotropy = false
  BoundaryEdges = -> [Sketch007]
  BoundaryOrder = [0,0,0,0,0,0,0,0,0,0]
  Degree = 3
  Iterations = 2
  MaximumDegree = 8
  MaximumSegments = 9
  PointsOnCurve = 15
  TolAngular = 0.01
  TolCurvature = 0.1
  Tolerance2d = 1e-05
  Tolerance3d = 0.0001
FEATURE [Part::Cut] Cut
  Base = -> Surface
  Tool = -> Surface001
FEATURE [Part::Cut] Cut001  label="Rotor_Surface"
  Base = -> Cut
  Tool = -> Surface002
FEATURE [Sketcher::SketchObject] Sketch  label="MagnetSketch2"
  ExternalGeometry = -> [Sketch007]
  MapMode = 5
  Support = -> [XY_Plane]
  expr: Constraints[17] = Variables.magnetHeight
  expr: Constraints[16] = Variables.magnetWidth
  expr: Constraints[15] = Variables.magnetAirgap
  sketch-geometry (6):
    g0: LineSegment StartX=11.3634 StartY=6.20129 StartZ=0 EndX=9.59566 EndY=4.43353 EndZ=0
    g1: LineSegment StartX=9.59566 StartY=4.43353 StartZ=0 EndX=13.1312 EndY=0.897993 EndZ=0
    g2: LineSegment StartX=13.1312 StartY=0.897993 StartZ=0 EndX=14.899 EndY=2.66576 EndZ=0
    g3: LineSegment StartX=14.899 StartY=2.66576 StartZ=0 EndX=11.3634 EndY=6.20129 EndZ=0
    g4: LineSegment [constr] StartX=9.56031 StartY=4.46888 StartZ=0 EndX=9.59566 EndY=4.43353 EndZ=0
    g5: LineSegment [constr] StartX=9.59566 StartY=4.43353 StartZ=0 EndX=9.56031 EndY=4.39817 EndZ=0
  constraints (18):
    c: Coincident(g0,g3)
    c: Coincident(g0,g1)
    c: Coincident(g1,g2)
    c: Coincident(g2,g3)
    c: Angle(g3,g2) = 1.5708
    c: Angle(g0,g3) = 1.5708
    c: Angle(g1,g0) = 1.5708
    c: Parallel(g1,g-4)
    c: PointOnObject(g4,g-3)
    c: Coincident(g4,g0)
    c: Angle(g4,g-3) = 1.5708
    c: Coincident(g5,g0)
    c: PointOnObject(g5,g-4)
    c: Angle(g4,g5) = 1.5708
    c: Equal(g4,g5)
    c: Distance(g4) = 0.05
    c: Distance(g1) = 5
    c: Distance(g2) = 2.5
FEATURE [Surface::Filling] Surface003  label="Magnet2"
  Anisotropy = false
  BoundaryEdges = -> [Sketch]
  BoundaryOrder = [0,0,0,0]
  Degree = 3
  Iterations = 2
  MaximumDegree = 8
  MaximumSegments = 9
  PointsOnCurve = 15
  TolAngular = 0.01
  TolCurvature = 0.1
  Tolerance2d = 1e-05
  Tolerance3d = 0.0001
FEATURE [Sketcher::SketchObject] Sketch008  label="MagnetSketch1"
  ExternalGeometry = -> [Sketch007]
  MapMode = 5
  Support = -> [XY_Plane]
  expr: Constraints[16] = Variables.magnetWidth
  expr: Constraints[17] = Variables.magnetHeight
  expr: Constraints[14] = Variables.magnetAirgap
  sketch-geometry (6):
    g0: LineSegment StartX=9.7581 StartY=11.57 StartZ=0 EndX=7.34328 EndY=10.923 EndZ=0
    g1: LineSegment StartX=7.34328 StartY=10.923 StartZ=0 EndX=8.63738 EndY=6.09332 EndZ=0
    g2: LineSegment StartX=8.63738 StartY=6.09332 StartZ=0 EndX=11.0522 EndY=6.74037 EndZ=0
    g3: LineSegment StartX=11.0522 StartY=6.74037 StartZ=0 EndX=9.7581 EndY=11.57 EndZ=0
    g4: LineSegment [constr] StartX=7.34328 StartY=10.923 StartZ=0 EndX=7.33034 EndY=10.9713 EndZ=0
    g5: LineSegment [constr] StartX=7.34328 StartY=10.923 StartZ=0 EndX=7.29499 EndY=10.91 EndZ=0
  constraints (18):
    c: Angle(g3,g2) = 1.5708
    c: Angle(g2,g1) = 1.5708
    c: Coincident(g0,g3)
    c: Coincident(g1,g0)
    c: Coincident(g1,g2)
    c: Coincident(g3,g2)
    c: Angle(g0,g3) = 1.5708
    c: PointOnObject(g5,g-3)
    c: PointOnObject(g4,g-4)
    c: Angle(g4,g-4) = 1.5708
    c: Angle(g-3,g5) = 1.5708
    c: Coincident(g0,g4)
    c: Coincident(g5,g0)
    c: Equal(g4,g5)
    c: Distance(g4) = 0.05
    c: Parallel(g1,g-3)
    c: Distance(g1) = 5
    c: Distance(g0) = 2.5
FEATURE [PartDesign::Body] Body  label="TopView"
  Group = -> [Sketch003,Sketch004,Sketch007,Sketch,Sketch008]
  Origin = -> Origin
FEATURE [Surface::Filling] Surface004  label="Magnet1"
  Anisotropy = false
  BoundaryEdges = -> [Sketch008]
  BoundaryOrder = [0,0,0,0]
  Degree = 3
  Iterations = 2
  MaximumDegree = 8
  MaximumSegments = 9
  PointsOnCurve = 15
  TolAngular = 0.01
  TolCurvature = 0.1
  Tolerance2d = 1e-05
  Tolerance3d = 0.0001
FEATURE [Part::MultiFuse] Fusion  label="Magnet_Surface"
  Shapes = -> [Surface004,Surface003]
FEATURE [Surface::Filling] Surface005  label="Magnet_Surface1"
  Anisotropy = false
  BoundaryEdges = -> [Sketch008]
  BoundaryOrder = [0,0,0,0]
  Degree = 3
  Iterations = 2
  MaximumDegree = 8
  MaximumSegments = 9
  PointsOnCurve = 15
  TolAngular = 0.01
  TolCurvature = 0.1
  Tolerance2d = 1e-05
  Tolerance3d = 0.0001
FEATURE [Surface::Filling] Surface006  label="Magnet_Surface2"
  Anisotropy = false
  BoundaryEdges = -> [Sketch]
  BoundaryOrder = [0,0,0,0]
  Degree = 3
  Iterations = 2
  MaximumDegree = 8
  MaximumSegments = 9
  PointsOnCurve = 15
  TolAngular = 0.01
  TolCurvature = 0.1
  Tolerance2d = 1e-05
  Tolerance3d = 0.0001
